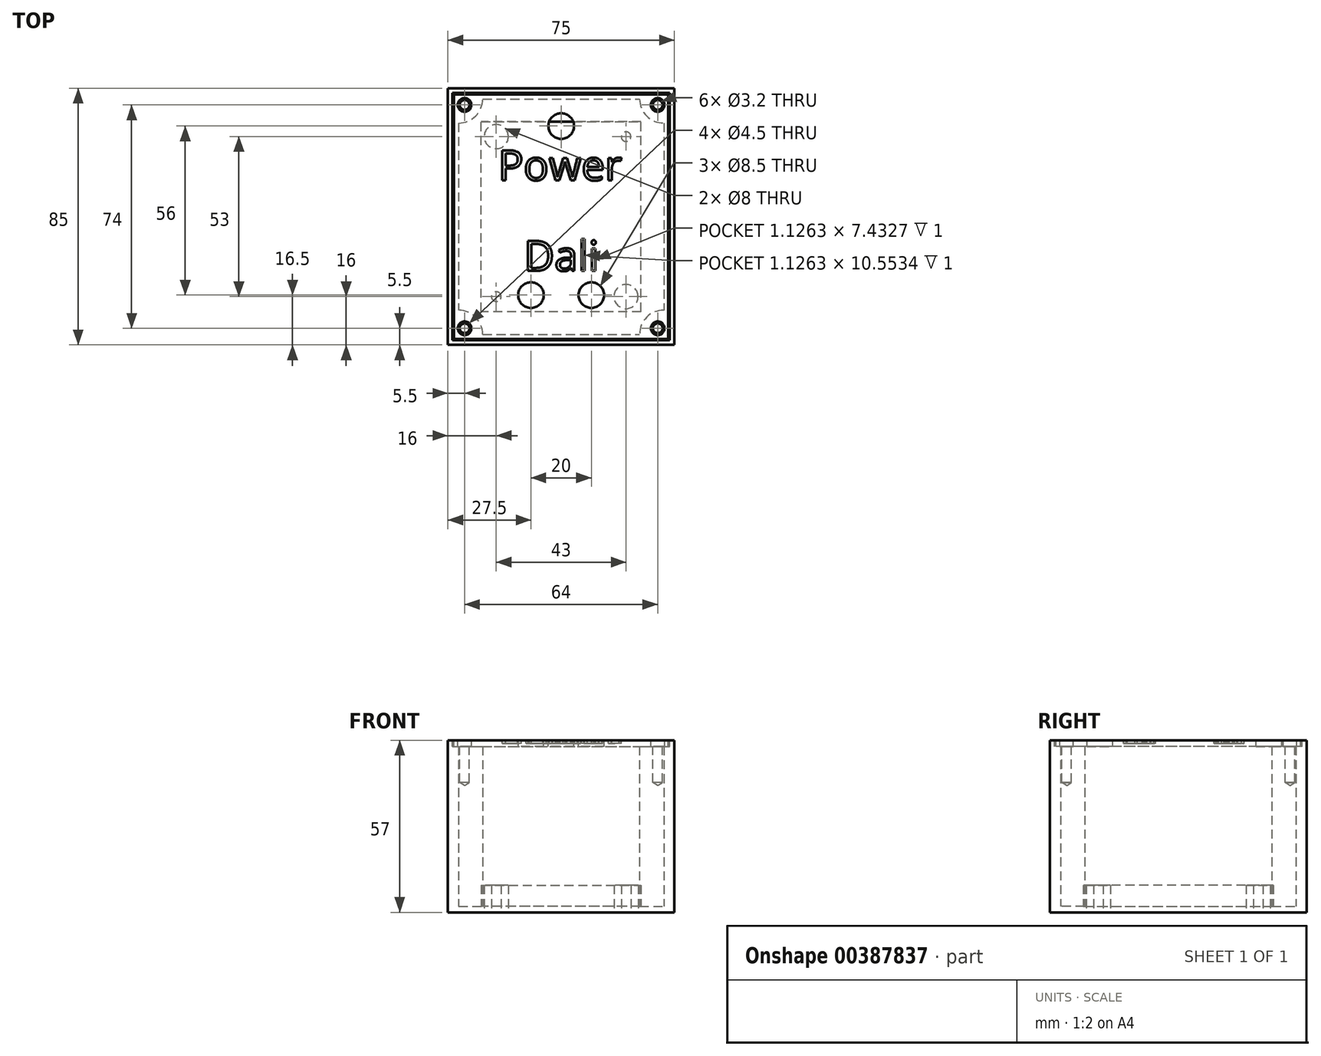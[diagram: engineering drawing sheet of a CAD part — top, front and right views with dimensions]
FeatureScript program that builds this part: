
annotation { "Feature Type Name" : "Feature", "Feature Type Description" : "" }
export const myFeature = defineFeature(function(context is Context, id is Id, definition is map)
    precondition{}
    {
        {
            var Q0;
            Q0=qCreatedBy(makeId("Top.planeOp"),FACE);
            var sketch = newSketch(context, id + "F0", { "sketchPlane" : qUnion([Q0])});
            skLineSegment(sketch, "E0.bottom", {"start": v(-26.5, 31.5) * mm, "end": v(26.5, 31.5) * mm});
            skLineSegment(sketch, "E0.top", {"start": v(-26.5, -31.5) * mm, "end": v(26.5, -31.5) * mm});
            skLineSegment(sketch, "E0.left", {"start": v(-26.5, 31.5) * mm, "end": v(-26.5, -31.5) * mm});
            skLineSegment(sketch, "E0.right", {"start": v(26.5, 31.5) * mm, "end": v(26.5, -31.5) * mm});
            skLineSegment(sketch, "E1.0", {"start": v(-28.5, -33.5) * mm, "end": v(28.5, -33.5) * mm, "construction": true});
            skLineSegment(sketch, "E1.1", {"start": v(-28.5, 33.5) * mm, "end": v(-28.5, -33.5) * mm, "construction": true});
            skLineSegment(sketch, "E1.2", {"start": v(-28.5, 33.5) * mm, "end": v(28.5, 33.5) * mm, "construction": true});
            skLineSegment(sketch, "E1.3", {"start": v(28.5, 33.5) * mm, "end": v(28.5, -33.5) * mm, "construction": true});
            skLineSegment(sketch, "E2.0", {"start": v(-37.5, 42.5) * mm, "end": v(37.5, 42.5) * mm});
            skLineSegment(sketch, "E2.1", {"start": v(-37.5, 42.5) * mm, "end": v(-37.5, -42.5) * mm});
            skLineSegment(sketch, "E2.2", {"start": v(-37.5, -42.5) * mm, "end": v(37.5, -42.5) * mm});
            skLineSegment(sketch, "E2.3", {"start": v(37.5, 42.5) * mm, "end": v(37.5, -42.5) * mm});
            skPoint(sketch, "E3", {"position": v(0, -42.5) * mm});
            skPoint(sketch, "E4", {"position": v(-37.5, 0) * mm});
            skPoint(sketch, "E5", {"position": v(-21.5, -26.5) * mm});
            skCircle(sketch, "E6", {"center": v(-21.5, -26.5) * mm, "radius": 4 * mm});
            skPoint(sketch, "E7.MirrorP", {"position": v(21.5, -26.5) * mm});
            skCircle(sketch, "E8.MirrorC", {"center": v(21.5, -26.5) * mm, "radius": 4 * mm});
            skPoint(sketch, "E9.MirrorP", {"position": v(21.5, 26.5) * mm});
            skCircle(sketch, "E10.MirrorC", {"center": v(21.5, 26.5) * mm, "radius": 4 * mm});
            skPoint(sketch, "E11.MirrorP", {"position": v(-21.5, 26.5) * mm});
            skCircle(sketch, "E12.MirrorC", {"center": v(-21.5, 26.5) * mm, "radius": 4 * mm});
            skPoint(sketch, "E13", {"position": v(-32, 37) * mm});
            skPoint(sketch, "E14.MirrorP", {"position": v(32, 37) * mm});
            skPoint(sketch, "E15.MirrorP", {"position": v(-32, -37) * mm});
            skPoint(sketch, "E16.MirrorP", {"position": v(32, -37) * mm});
            skLineSegment(sketch, "E17.0", {"start": v(-26, 39) * mm, "end": v(26, 39) * mm});
            skLineSegment(sketch, "E17.1", {"start": v(-34, 31) * mm, "end": v(-34, -31) * mm});
            skLineSegment(sketch, "E17.2", {"start": v(-26, -39) * mm, "end": v(26, -39) * mm});
            skLineSegment(sketch, "E17.3", {"start": v(34, 31) * mm, "end": v(34, -31) * mm});
            skArc(sketch, "E18", {"start": v(-26, 39) * mm, "mid": v(-28.34, 33.34) * mm, "end": v(-34, 31) * mm});
            skArc(sketch, "E19.MirrorCS", {"start": v(26, 39) * mm, "mid": v(28.34, 33.34) * mm, "end": v(34, 31) * mm});
            skArc(sketch, "E20.MirrorCS", {"start": v(-26, -39) * mm, "mid": v(-28.34, -33.34) * mm, "end": v(-34, -31) * mm});
            skArc(sketch, "E21.MirrorCS", {"start": v(26, -39) * mm, "mid": v(28.34, -33.34) * mm, "end": v(34, -31) * mm});
            skSolve(sketch);
        }
        {
            var Q0;
            Q0=makeQuery(id+"F0.imprint","IMPRINT",FACE,{"disambiguationData":[TD([[makeQuery(id+"F0.imprint","IMPRINT",EDGE,{"derivedFrom":sQuery(id+"F0.wireOp",EDGE,"E0.bottom")}),1.0]])]});
            var Q1;
            Q1=makeQuery(id+"F0.imprint","IMPRINT",FACE,{"disambiguationData":[TD([[makeQuery(id+"F0.imprint","IMPRINT",EDGE,{"derivedFrom":sQuery(id+"F0.wireOp",EDGE,"E0.bottom")}),-1.0]])]});
            var Q2;
            Q2=makeQuery(id+"F0.imprint","IMPRINT",FACE,{"disambiguationData":[TD([[makeQuery(id+"F0.imprint","IMPRINT",EDGE,{"derivedFrom":sQuery(id+"F0.wireOp",EDGE,"E12.MirrorC")}),-1.0]])]});
            var Q3;
            Q3=makeQuery(id+"F0.imprint","IMPRINT",FACE,{"disambiguationData":[TD([[makeQuery(id+"F0.imprint","IMPRINT",EDGE,{"derivedFrom":sQuery(id+"F0.wireOp",EDGE,"E10.MirrorC")}),1.0]])]});
            var Q4;
            Q4=makeQuery(id+"F0.imprint","IMPRINT",FACE,{"disambiguationData":[TD([[makeQuery(id+"F0.imprint","IMPRINT",EDGE,{"derivedFrom":sQuery(id+"F0.wireOp",EDGE,"E8.MirrorC")}),-1.0]])]});
            var Q5;
            Q5=makeQuery(id+"F0.imprint","IMPRINT",FACE,{"disambiguationData":[TD([[makeQuery(id+"F0.imprint","IMPRINT",EDGE,{"derivedFrom":sQuery(id+"F0.wireOp",EDGE,"E6")}),1.0]])]});
            var Q6;
            Q6=makeQuery(id+"F0.imprint","IMPRINT",FACE,{"disambiguationData":[TD([[makeQuery(id+"F0.imprint","IMPRINT",EDGE,{"derivedFrom":sQuery(id+"F0.wireOp",EDGE,"E1.0")}),-1.0]])]});
            var Q7;
            Q7=makeQuery(id+"F0.imprint","IMPRINT",FACE,{"disambiguationData":[TD([[makeQuery(id+"F0.imprint","IMPRINT",EDGE,{"derivedFrom":sQuery(id+"F0.wireOp",EDGE,"E2.0")}),-1.0]])]});
            extrude(context, id + "F1", {"entities" : qUnion([Q0, Q1, Q2, Q3, Q4, Q5, Q6, Q7]), "depth" : 2 * mm});
        }
        {
            var Q0;
            Q0=makeQuery(id+"F0.imprint","IMPRINT",FACE,{"disambiguationData":[TD([[makeQuery(id+"F0.imprint","IMPRINT",EDGE,{"derivedFrom":sQuery(id+"F0.wireOp",EDGE,"E2.0")}),-1.0]])]});
            extrude(context, id + "F2", {"entities" : qUnion([Q0]), "operationType" : NewBodyOperationType.ADD, "depth" : 57 * mm});
        }
        {
            var Q0;
            Q0=makeQuery(id+"F0.imprint","IMPRINT",FACE,{"disambiguationData":[TD([[makeQuery(id+"F0.imprint","IMPRINT",EDGE,{"derivedFrom":sQuery(id+"F0.wireOp",EDGE,"E6")}),1.0]])]});
            var Q1;
            Q1=makeQuery(id+"F0.imprint","IMPRINT",FACE,{"disambiguationData":[TD([[makeQuery(id+"F0.imprint","IMPRINT",EDGE,{"derivedFrom":sQuery(id+"F0.wireOp",EDGE,"E8.MirrorC")}),-1.0]])]});
            var Q2;
            Q2=makeQuery(id+"F0.imprint","IMPRINT",FACE,{"disambiguationData":[TD([[makeQuery(id+"F0.imprint","IMPRINT",EDGE,{"derivedFrom":sQuery(id+"F0.wireOp",EDGE,"E10.MirrorC")}),1.0]])]});
            var Q3;
            Q3=makeQuery(id+"F0.imprint","IMPRINT",FACE,{"disambiguationData":[TD([[makeQuery(id+"F0.imprint","IMPRINT",EDGE,{"derivedFrom":sQuery(id+"F0.wireOp",EDGE,"E12.MirrorC")}),-1.0]])]});
            extrude(context, id + "F3", {"entities" : qUnion([Q0, Q1, Q2, Q3]), "operationType" : NewBodyOperationType.ADD, "depth" : 9 * mm});
        }
        {
            var Q0;
            Q0=makeQuery(id+"F2.opExtrude","CAP_FACE",FACE,{"disambiguationData":[OSD([sQuery(id+"F0.wireOp",EDGE,"E2.0"),sQuery(id+"F0.wireOp",EDGE,"E2.1"),sQuery(id+"F0.wireOp",EDGE,"E2.2"),sQuery(id+"F0.wireOp",EDGE,"E2.3"),sQuery(id+"F0.wireOp",EDGE,"E17.0"),sQuery(id+"F0.wireOp",EDGE,"E17.1"),sQuery(id+"F0.wireOp",EDGE,"E17.2"),sQuery(id+"F0.wireOp",EDGE,"E17.3"),sQuery(id+"F0.wireOp",EDGE,"E18"),sQuery(id+"F0.wireOp",EDGE,"E19.MirrorCS"),sQuery(id+"F0.wireOp",EDGE,"E20.MirrorCS"),sQuery(id+"F0.wireOp",EDGE,"E21.MirrorCS")])],"isStart":false});
            var sketch = newSketch(context, id + "F4", { "sketchPlane" : qUnion([Q0])});
            skLineSegment(sketch, "E22.0", {"start": v(36, 41) * mm, "end": v(36, -41) * mm});
            skLineSegment(sketch, "E22.1", {"start": v(-36, 41) * mm, "end": v(36, 41) * mm});
            skLineSegment(sketch, "E22.2", {"start": v(-36, 41) * mm, "end": v(-36, -41) * mm});
            skLineSegment(sketch, "E22.3", {"start": v(-36, -41) * mm, "end": v(36, -41) * mm});
            skSolve(sketch);
        }
        {
            var Q0;
            Q0=makeQuery(id+"F4.imprint","IMPRINT",FACE,{"disambiguationData":[TD([[makeQuery(id+"F4.imprint","IMPRINT",EDGE,{"derivedFrom":sQuery(id+"F4.wireOp",EDGE,"E22.0")}),-1.0]])]});
            extrude(context, id + "F5", {"entities" : qUnion([Q0]), "operationType" : NewBodyOperationType.REMOVE, "oppositeDirection" : true, "depth" : 2 * mm});
        }
        {
            var Q0;
            Q0=sQuery(id+"F0.wireOp",VERTEX,"E11.MirrorP");
            var Q1;
            Q1=sQuery(id+"F0.wireOp",VERTEX,"E9.MirrorP");
            var Q2;
            Q2=sQuery(id+"F0.wireOp",VERTEX,"E5");
            var Q3;
            Q3=sQuery(id+"F0.wireOp",VERTEX,"E7.MirrorP");
            var Q4;
            Q4=makeQuery(id+"F1.opExtrude","SWEPT_BODY",BODY,{"disambiguationData":[OSD([sQuery(id+"F0.wireOp",EDGE,"E2.0"),sQuery(id+"F0.wireOp",EDGE,"E2.1"),sQuery(id+"F0.wireOp",EDGE,"E2.2"),sQuery(id+"F0.wireOp",EDGE,"E2.3")])]});
            hole(context, id + "F6", {"style" : HoleStyle.SIMPLE, "endStyle" : HoleEndStyle.THROUGH, "oppositeDirection" : true, "holeDiameter" : 3.2 * mm, "tappedDepth" : 12 * mm, "tapClearance" : 3, "locations" : qUnion([Q0, Q1, Q2, Q3]), "scope" : qUnion([Q4])});
        }
        {
            var Q0;
            Q0=makeQuery(id+"F5.boolean.opBoolean","COPY",FACE,{"derivedFrom":makeQuery(id+"F5.opExtrude","CAP_FACE",FACE,{"disambiguationData":[OSD([sQuery(id+"F0.wireOp",EDGE,"E17.0"),sQuery(id+"F0.wireOp",EDGE,"E17.1"),sQuery(id+"F0.wireOp",EDGE,"E17.2"),sQuery(id+"F0.wireOp",EDGE,"E17.3"),sQuery(id+"F0.wireOp",EDGE,"E18"),sQuery(id+"F0.wireOp",EDGE,"E19.MirrorCS"),sQuery(id+"F0.wireOp",EDGE,"E20.MirrorCS"),sQuery(id+"F0.wireOp",EDGE,"E21.MirrorCS"),sQuery(id+"F4.wireOp",EDGE,"E22.0"),sQuery(id+"F4.wireOp",EDGE,"E22.1"),sQuery(id+"F4.wireOp",EDGE,"E22.2"),sQuery(id+"F4.wireOp",EDGE,"E22.3")])],"isStart":false})});
            var sketch = newSketch(context, id + "F7", { "sketchPlane" : qUnion([Q0])});
            skPoint(sketch, "E23.0", {"position": v(-32, -37) * mm});
            skPoint(sketch, "E24.0", {"position": v(-32, 37) * mm});
            skPoint(sketch, "E25.0", {"position": v(32, 37) * mm});
            skPoint(sketch, "E26.0", {"position": v(32, -37) * mm});
            skSolve(sketch);
        }
        {
            var Q0;
            Q0=sQuery(id+"F7.wireOp",VERTEX,"E23.0");
            var Q1;
            Q1=sQuery(id+"F7.wireOp",VERTEX,"E24.0");
            var Q2;
            Q2=sQuery(id+"F7.wireOp",VERTEX,"E25.0");
            var Q3;
            Q3=sQuery(id+"F7.wireOp",VERTEX,"E26.0");
            var Q4;
            Q4=makeQuery(id+"F1.opExtrude","SWEPT_BODY",BODY,{"disambiguationData":[OSD([sQuery(id+"F0.wireOp",EDGE,"E2.0"),sQuery(id+"F0.wireOp",EDGE,"E2.1"),sQuery(id+"F0.wireOp",EDGE,"E2.2"),sQuery(id+"F0.wireOp",EDGE,"E2.3")])]});
            hole(context, id + "F8", {"style" : HoleStyle.SIMPLE, "endStyle" : HoleEndStyle.BLIND, "holeDiameter" : 3.2 * mm, "holeDepth" : 12 * mm, "tappedDepth" : 12 * mm, "tapClearance" : 3, "locations" : qUnion([Q0, Q1, Q2, Q3]), "scope" : qUnion([Q4])});
        }
        {
            var Q0;
            Q0=makeQuery(id+"F2.opExtrude","CAP_FACE",FACE,{"disambiguationData":[OSD([sQuery(id+"F0.wireOp",EDGE,"E2.0"),sQuery(id+"F0.wireOp",EDGE,"E2.1"),sQuery(id+"F0.wireOp",EDGE,"E2.2"),sQuery(id+"F0.wireOp",EDGE,"E2.3"),sQuery(id+"F0.wireOp",EDGE,"E17.0"),sQuery(id+"F0.wireOp",EDGE,"E17.1"),sQuery(id+"F0.wireOp",EDGE,"E17.2"),sQuery(id+"F0.wireOp",EDGE,"E17.3"),sQuery(id+"F0.wireOp",EDGE,"E18"),sQuery(id+"F0.wireOp",EDGE,"E19.MirrorCS"),sQuery(id+"F0.wireOp",EDGE,"E20.MirrorCS"),sQuery(id+"F0.wireOp",EDGE,"E21.MirrorCS")])],"isStart":false});
            var sketch = newSketch(context, id + "F9", { "sketchPlane" : qUnion([Q0])});
            skLineSegment(sketch, "E27.0", {"start": v(-35.5, 40.5) * mm, "end": v(-35.5, -40.5) * mm});
            skLineSegment(sketch, "E27.1", {"start": v(-35.5, 40.5) * mm, "end": v(35.5, 40.5) * mm});
            skLineSegment(sketch, "E27.2", {"start": v(35.5, 40.5) * mm, "end": v(35.5, -40.5) * mm});
            skLineSegment(sketch, "E27.3", {"start": v(-35.5, -40.5) * mm, "end": v(35.5, -40.5) * mm});
            skPoint(sketch, "E28.0", {"position": v(-32, -37) * mm});
            skPoint(sketch, "E29.0", {"position": v(-32, 37) * mm});
            skPoint(sketch, "E30.0", {"position": v(32, 37) * mm});
            skPoint(sketch, "E31.0", {"position": v(32, -37) * mm});
            skSolve(sketch);
        }
        {
            var Q0;
            Q0 = qSketchRegion(id + "F9", true);
            extrude(context, id + "F10", {"entities" : qUnion([Q0]), "oppositeDirection" : true, "depth" : 2 * mm});
        }
        {
            var Q0;
            Q0=sQuery(id+"F9.wireOp",VERTEX,"E29.0");
            var Q1;
            Q1=sQuery(id+"F9.wireOp",VERTEX,"E30.0");
            var Q2;
            Q2=sQuery(id+"F9.wireOp",VERTEX,"E31.0");
            var Q3;
            Q3=sQuery(id+"F9.wireOp",VERTEX,"E28.0");
            var Q4;
            Q4=makeQuery(id+"F10.opExtrude","SWEPT_BODY",BODY,{"disambiguationData":[OSD([sQuery(id+"F9.wireOp",EDGE,"E27.0"),sQuery(id+"F9.wireOp",EDGE,"E27.1"),sQuery(id+"F9.wireOp",EDGE,"E27.2"),sQuery(id+"F9.wireOp",EDGE,"E27.3")])]});
            hole(context, id + "F11", {"style" : HoleStyle.SIMPLE, "endStyle" : HoleEndStyle.BLIND, "holeDiameter" : 4.5 * mm, "holeDepth" : 12 * mm, "tappedDepth" : 12 * mm, "tapClearance" : 3, "locations" : qUnion([Q0, Q1, Q2, Q3]), "scope" : qUnion([Q4])});
        }
        {
            var Q0;
            Q0=makeQuery(id+"F9.imprint","IMPRINT",FACE,{"disambiguationData":[TD([[makeQuery(id+"F9.imprint","IMPRINT",EDGE,{"derivedFrom":sQuery(id+"F9.wireOp",EDGE,"E27.0")}),1.0]])]});
            var sketch = newSketch(context, id + "F12", { "sketchPlane" : qUnion([Q0])});
            skPoint(sketch, "E32", {"position": v(0, 30) * mm});
            skPoint(sketch, "E33", {"position": v(-10, -26) * mm});
            skPoint(sketch, "E34", {"position": v(10, -26) * mm});
            skText(sketch, "E35", { "text": "Power", "fontName": "OpenSans-Regular.ttf"});
            skText(sketch, "E36", { "text": "Dali\n", "fontName": "OpenSans-Regular.ttf"});
            const initialGuessF12  = {"E35": [-0.02086, 0.012, 1, 0, 0.01], "E36": [-0.01235, -0.018, 1, 0, 0.01]};
            skSetInitialGuess(sketch, initialGuessF12);
            skSolve(sketch);
        }
        {
            var Q0;
            Q0=sQuery(id+"F12.wireOp",VERTEX,"E32");
            var Q1;
            Q1=sQuery(id+"F12.wireOp",VERTEX,"E33");
            var Q2;
            Q2=sQuery(id+"F12.wireOp",VERTEX,"E34");
            var Q3;
            Q3=makeQuery(id+"F10.opExtrude","SWEPT_BODY",BODY,{"disambiguationData":[OSD([sQuery(id+"F9.wireOp",EDGE,"E27.0"),sQuery(id+"F9.wireOp",EDGE,"E27.1"),sQuery(id+"F9.wireOp",EDGE,"E27.2"),sQuery(id+"F9.wireOp",EDGE,"E27.3")])]});
            hole(context, id + "F13", {"style" : HoleStyle.SIMPLE, "endStyle" : HoleEndStyle.THROUGH, "holeDiameter" : 8.5 * mm, "tappedDepth" : 12 * mm, "tapClearance" : 3, "locations" : qUnion([Q0, Q1, Q2]), "scope" : qUnion([Q3])});
        }
        {
            var Q0;
            Q0 = qSketchRegion(id + "F12", true);
            extrude(context, id + "F14", {"entities" : qUnion([Q0]), "operationType" : NewBodyOperationType.REMOVE, "oppositeDirection" : true, "depth" : 1 * mm});
        }
    });
